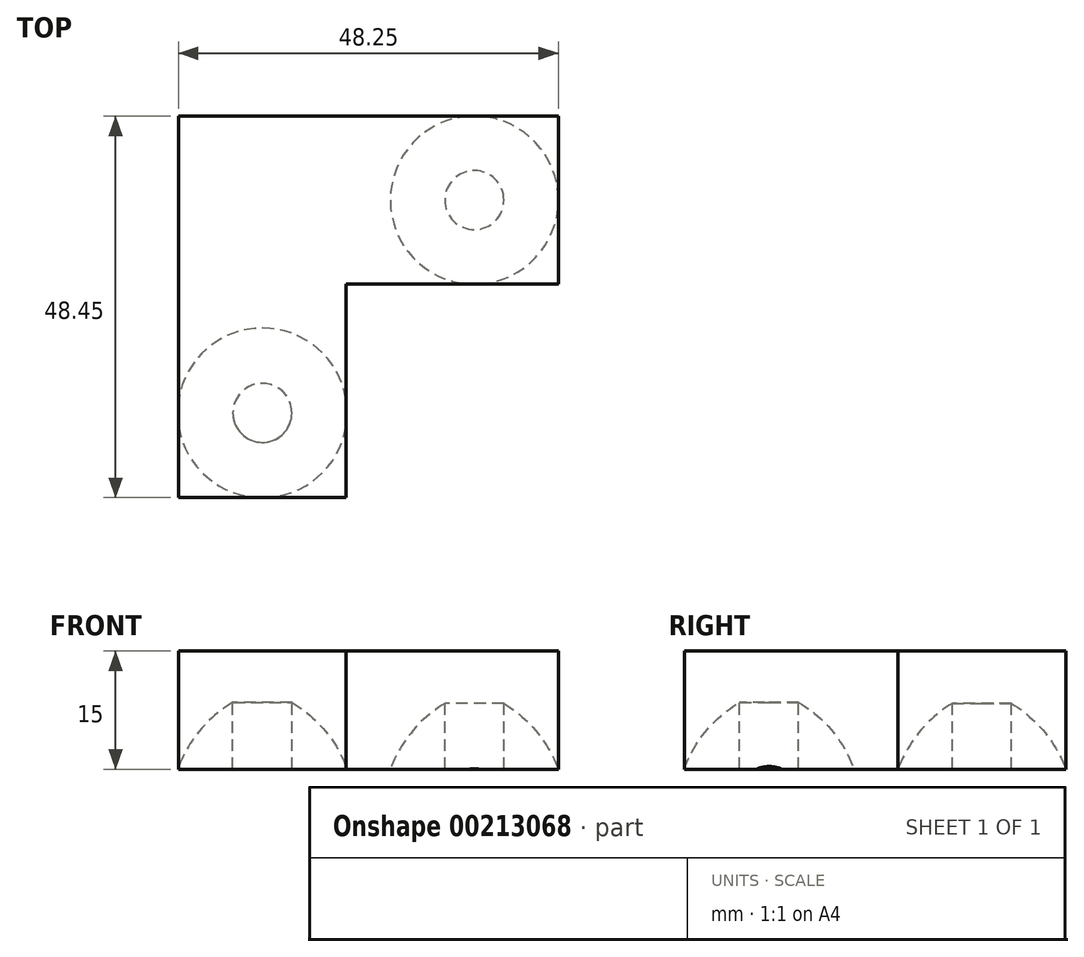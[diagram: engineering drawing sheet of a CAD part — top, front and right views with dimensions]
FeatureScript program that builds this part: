
annotation { "Feature Type Name" : "Feature", "Feature Type Description" : "" }
export const myFeature = defineFeature(function(context is Context, id is Id, definition is map)
    precondition{}
    {
        {
            var Q0;
            Q0=qCreatedBy(makeId("Top.planeOp"),FACE);
            var sketch = newSketch(context, id + "F0", { "sketchPlane" : qUnion([Q0])});
            skLineSegment(sketch, "E0.bottom", {"start": v(-10.65, 10.65) * mm, "end": v(37.6, 10.65) * mm});
            skLineSegment(sketch, "E0.top", {"start": v(-10.65, -10.65) * mm, "end": v(37.6, -10.65) * mm});
            skLineSegment(sketch, "E0.left", {"start": v(-10.65, 10.65) * mm, "end": v(-10.65, -10.65) * mm});
            skLineSegment(sketch, "E0.right", {"start": v(37.6, 10.65) * mm, "end": v(37.6, -10.65) * mm});
            skLineSegment(sketch, "E1.bottom", {"start": v(-10.65, 10.65) * mm, "end": v(10.65, 10.65) * mm});
            skLineSegment(sketch, "E1.top", {"start": v(-10.65, -37.8) * mm, "end": v(10.65, -37.8) * mm});
            skLineSegment(sketch, "E1.left", {"start": v(-10.65, 10.65) * mm, "end": v(-10.65, -37.8) * mm});
            skLineSegment(sketch, "E1.right", {"start": v(10.65, 10.65) * mm, "end": v(10.65, -37.8) * mm});
            skPoint(sketch, "E2", {"position": v(0, 10.65) * mm});
            skPoint(sketch, "E3", {"position": v(-10.65, 0) * mm});
            skCircle(sketch, "E4", {"center": v(26.93, 0) * mm, "radius": 10.63 * mm});
            skPoint(sketch, "E5", {"position": v(16.3, 0) * mm});
            skLineSegment(sketch, "E6", {"start": v(0, 0) * mm, "end": v(16.3, 0) * mm});
            skCircle(sketch, "E7", {"center": v(0, -27.13) * mm, "radius": 10.63 * mm});
            skPoint(sketch, "E8", {"position": v(0, -16.5) * mm});
            skLineSegment(sketch, "E9", {"start": v(0, -16.5) * mm, "end": v(0, 0) * mm});
            skLineSegment(sketch, "E10", {"start": v(0, -27.13) * mm, "end": v(0, -23.38) * mm});
            skLineSegment(sketch, "E11", {"start": v(-10.65, 0) * mm, "end": v(16.3, 0) * mm});
            skSolve(sketch);
        }
        {
            var Q0;
            Q0 = qSketchRegion(id + "F0", true);
            var Q1;
            Q1=makeQuery(id+"F0.imprint","IMPRINT",FACE,{"disambiguationData":[TD([[makeQuery(id+"F0.imprint","IMPRINT",EDGE,{"derivedFrom":sQuery(id+"F0.wireOp",EDGE,"E7")}),1.0]])]});
            var Q2;
            Q2=makeQuery(id+"F0.imprint","IMPRINT",FACE,{"disambiguationData":[TD([[makeQuery(id+"F0.imprint","IMPRINT",EDGE,{"derivedFrom":sQuery(id+"F0.wireOp",EDGE,"E4")}),1.0]])]});
            extrude(context, id + "F1", {"entities" : qUnion([Q0, Q1, Q2]), "depth" : 15 * mm});
        }
        {
            var Q0;
            Q0=qCreatedBy(makeId("Right.planeOp"),FACE);
            var sketch = newSketch(context, id + "F2", { "sketchPlane" : qUnion([Q0])});
            skArc(sketch, "E12", {"start": v(-30.77, 8.5) * mm, "mid": v(-35.03, 4.86) * mm, "end": v(-37.8, 0) * mm});
            skLineSegment(sketch, "E13", {"start": v(-30.77, 0) * mm, "end": v(-37.8, 0) * mm});
            skLineSegment(sketch, "E14", {"start": v(-27.02, 0) * mm, "end": v(-27.02, 15) * mm, "construction": true});
            skLineSegment(sketch, "E15", {"start": v(-30.77, 0) * mm, "end": v(-30.77, 8.5) * mm});
            skPoint(sketch, "E16.orphan", {"position": v(-27.13, 10.1) * mm});
            skSolve(sketch);
        }
        {
            var Q0;
            Q0 = qSketchRegion(id + "F2", true);
            var Q1;
            Q1=sQuery(id+"F2.wireOp",EDGE,"E14");
            revolve(context, id + "F3", {"operationType" : NewBodyOperationType.REMOVE, "entities" : qUnion([Q0]), "axis" : qUnion([Q1]), "revolveType" : RevolveType.FULL, "oppositeDirection" : true});
        }
        {
            var Q0;
            Q0=qCreatedBy(makeId("Front.planeOp"),FACE);
            var sketch = newSketch(context, id + "F4", { "sketchPlane" : qUnion([Q0])});
            skArc(sketch, "E17", {"start": v(37.6, 0) * mm, "mid": v(34.85, 4.77) * mm, "end": v(30.68, 8.37) * mm});
            skLineSegment(sketch, "E18", {"start": v(26.93, 0) * mm, "end": v(30.68, 0) * mm});
            skLineSegment(sketch, "E19", {"start": v(30.68, 0) * mm, "end": v(30.68, 8.37) * mm});
            skLineSegment(sketch, "E20", {"start": v(30.68, 0) * mm, "end": v(37.6, 0) * mm});
            skLineSegment(sketch, "E21", {"start": v(26.93, 0) * mm, "end": v(26.93, 12.46) * mm, "construction": true});
            skSolve(sketch);
        }
        {
            var Q0;
            Q0 = qSketchRegion(id + "F4", true);
            var Q1;
            Q1=sQuery(id+"F4.wireOp",EDGE,"E21");
            revolve(context, id + "F5", {"operationType" : NewBodyOperationType.REMOVE, "entities" : qUnion([Q0]), "axis" : qUnion([Q1]), "revolveType" : RevolveType.FULL, "oppositeDirection" : true});
        }
    });
